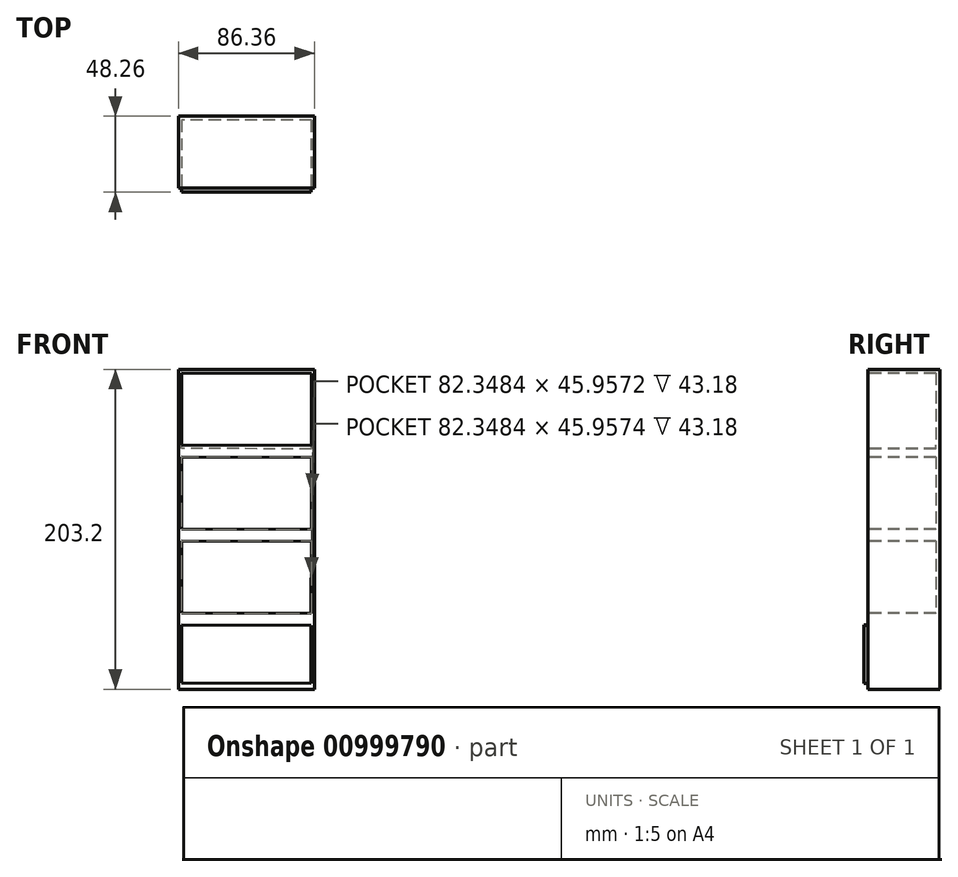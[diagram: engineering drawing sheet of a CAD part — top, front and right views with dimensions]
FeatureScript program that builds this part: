
annotation { "Feature Type Name" : "Feature", "Feature Type Description" : "" }
export const myFeature = defineFeature(function(context is Context, id is Id, definition is map)
    precondition{}
    {
        {
            var Q0;
            Q0=qCreatedBy(makeId("Front.planeOp"),FACE);
            var sketch = newSketch(context, id + "F0", { "sketchPlane" : qUnion([Q0])});
            skLineSegment(sketch, "E0.bottom", {"start": v(0, 0) * mm, "end": v(86.36, 0) * mm});
            skLineSegment(sketch, "E0.top", {"start": v(0, -203.2) * mm, "end": v(86.36, -203.2) * mm});
            skLineSegment(sketch, "E0.left", {"start": v(0, 0) * mm, "end": v(0, -203.2) * mm});
            skLineSegment(sketch, "E0.right", {"start": v(86.36, 0) * mm, "end": v(86.36, -203.2) * mm});
            skSolve(sketch);
        }
        {
            var Q0;
            Q0=makeQuery(id+"F0.imprint","IMPRINT",FACE,{"disambiguationData":[TD([[makeQuery(id+"F0.imprint","IMPRINT",EDGE,{"derivedFrom":sQuery(id+"F0.wireOp",EDGE,"E0.bottom")}),-1.0]])]});
            extrude(context, id + "F1", {"entities" : qUnion([Q0]), "oppositeDirection" : true, "depth" : 45.72 * mm, "offsetDistance" : 25.4 * mm});
        }
        {
            var Q0;
            Q0=makeQuery(id+"F1.opExtrude","CAP_FACE",FACE,{"disambiguationData":[OSD([sQuery(id+"F0.wireOp",EDGE,"E0.bottom"),sQuery(id+"F0.wireOp",EDGE,"E0.top"),sQuery(id+"F0.wireOp",EDGE,"E0.left"),sQuery(id+"F0.wireOp",EDGE,"E0.right")])],"isStart":true});
            var sketch = newSketch(context, id + "F2", { "sketchPlane" : qUnion([Q0])});
            skLineSegment(sketch, "E1", {"start": v(2.1, -2.3) * mm, "end": v(2.1, -48.02) * mm});
            skLineSegment(sketch, "E2", {"start": v(84.45, -2.54) * mm, "end": v(84.45, -48.26) * mm});
            skLineSegment(sketch, "E3", {"start": v(84.45, -48.26) * mm, "end": v(2.1, -48.02) * mm});
            skLineSegment(sketch, "E4", {"start": v(2.1, -2.3) * mm, "end": v(84.45, -2.54) * mm});
            skLineSegment(sketch, "E5", {"start": v(84.45, -55.88) * mm, "end": v(2.1, -55.64) * mm});
            skLineSegment(sketch, "E6", {"start": v(2.1, -55.64) * mm, "end": v(2.1, -101.36) * mm});
            skLineSegment(sketch, "E7", {"start": v(84.45, -55.88) * mm, "end": v(84.45, -101.6) * mm});
            skPoint(sketch, "E7.endSnap0", {"position": v(86.36, -101.6) * mm});
            skLineSegment(sketch, "E8", {"start": v(84.45, -101.6) * mm, "end": v(2.1, -101.36) * mm});
            skLineSegment(sketch, "E9", {"start": v(84.45, -109.22) * mm, "end": v(2.1, -108.98) * mm});
            skLineSegment(sketch, "E10", {"start": v(2.1, -108.98) * mm, "end": v(2.1, -154.7) * mm});
            skLineSegment(sketch, "E11", {"start": v(84.45, -109.22) * mm, "end": v(84.31, -154.94) * mm});
            skLineSegment(sketch, "E12", {"start": v(84.31, -154.94) * mm, "end": v(2.1, -154.7) * mm});
            skLineSegment(sketch, "E13", {"start": v(84.3, -162.56) * mm, "end": v(2.1, -162.32) * mm});
            skLineSegment(sketch, "E14", {"start": v(2.1, -162.32) * mm, "end": v(2.1, -199.15) * mm});
            skLineSegment(sketch, "E15", {"start": v(84.3, -162.56) * mm, "end": v(84.19, -199.39) * mm});
            skLineSegment(sketch, "E16", {"start": v(84.19, -199.39) * mm, "end": v(2.1, -199.15) * mm});
            skSolve(sketch);
        }
        {
            var Q0;
            Q0=makeQuery(id+"F2.imprint","IMPRINT",FACE,{"disambiguationData":[TD([[makeQuery(id+"F2.imprint","IMPRINT",EDGE,{"derivedFrom":sQuery(id+"F2.wireOp",EDGE,"E1")}),1.0]])]});
            var Q1;
            Q1=makeQuery(id+"F2.imprint","IMPRINT",FACE,{"disambiguationData":[TD([[makeQuery(id+"F2.imprint","IMPRINT",EDGE,{"derivedFrom":sQuery(id+"F2.wireOp",EDGE,"E5")}),1.0]])]});
            var Q2;
            Q2=makeQuery(id+"F2.imprint","IMPRINT",FACE,{"disambiguationData":[TD([[makeQuery(id+"F2.imprint","IMPRINT",EDGE,{"derivedFrom":sQuery(id+"F2.wireOp",EDGE,"E9")}),1.0]])]});
            extrude(context, id + "F3", {"entities" : qUnion([Q0, Q1, Q2]), "operationType" : NewBodyOperationType.REMOVE, "oppositeDirection" : true, "depth" : 43.18 * mm, "offsetDistance" : 25.4 * mm});
        }
        {
            var Q0;
            Q0=makeQuery(id+"F1.opExtrude","CAP_FACE",FACE,{"disambiguationData":[OSD([sQuery(id+"F0.wireOp",EDGE,"E0.bottom"),sQuery(id+"F0.wireOp",EDGE,"E0.top"),sQuery(id+"F0.wireOp",EDGE,"E0.left"),sQuery(id+"F0.wireOp",EDGE,"E0.right")])],"isStart":true});
            var sketch = newSketch(context, id + "F4", { "sketchPlane" : qUnion([Q0])});
            skLineSegment(sketch, "E17", {"start": v(84.3, -162.56) * mm, "end": v(2.1, -162.32) * mm});
            skLineSegment(sketch, "E18", {"start": v(2.1, -162.32) * mm, "end": v(2.1, -199.15) * mm});
            skLineSegment(sketch, "E19", {"start": v(84.3, -162.56) * mm, "end": v(84.3, -199.39) * mm});
            skLineSegment(sketch, "E20", {"start": v(84.3, -199.39) * mm, "end": v(2.1, -199.15) * mm});
            skSolve(sketch);
        }
        {
            var Q0;
            Q0=makeQuery(id+"F4.imprint","IMPRINT",FACE,{"disambiguationData":[TD([[makeQuery(id+"F4.imprint","IMPRINT",EDGE,{"derivedFrom":sQuery(id+"F4.wireOp",EDGE,"E17")}),1.0]])]});
            extrude(context, id + "F5", {"entities" : qUnion([Q0]), "operationType" : NewBodyOperationType.ADD, "depth" : 2.54 * mm, "offsetDistance" : 25.4 * mm});
        }
        {
            var Q0;
            Q0=makeQuery(id+"F3.boolean.opBoolean","COPY",FACE,{"derivedFrom":makeQuery(id+"F3.opExtrude","SWEPT_FACE",FACE,{"disambiguationData":[OSD([sQuery(id+"F2.wireOp",EDGE,"E3")])]})});
            var sketch = newSketch(context, id + "F6", { "sketchPlane" : qUnion([Q0])});
            skLineSegment(sketch, "E21", {"start": v(2.24, 43.18) * mm, "end": v(2.24, 0.5) * mm});
            skLineSegment(sketch, "E22", {"start": v(2.24, 0.5) * mm, "end": v(84.58, 0.5) * mm});
            skLineSegment(sketch, "E23", {"start": v(84.58, 0.5) * mm, "end": v(84.58, 43.18) * mm});
            skLineSegment(sketch, "E24", {"start": v(84.58, 43.18) * mm, "end": v(2.24, 43.18) * mm});
            skSolve(sketch);
        }
        {
            var Q0;
            Q0=makeQuery(id+"F6.imprint","IMPRINT",FACE,{"disambiguationData":[TD([[makeQuery(id+"F6.imprint","IMPRINT",EDGE,{"derivedFrom":sQuery(id+"F6.wireOp",EDGE,"E21")}),1.0]])]});
            extrude(context, id + "F7", {"entities" : qUnion([Q0]), "operationType" : NewBodyOperationType.REMOVE, "oppositeDirection" : true, "depth" : 2.3 * mm, "offsetDistance" : 25.4 * mm});
        }
    });
